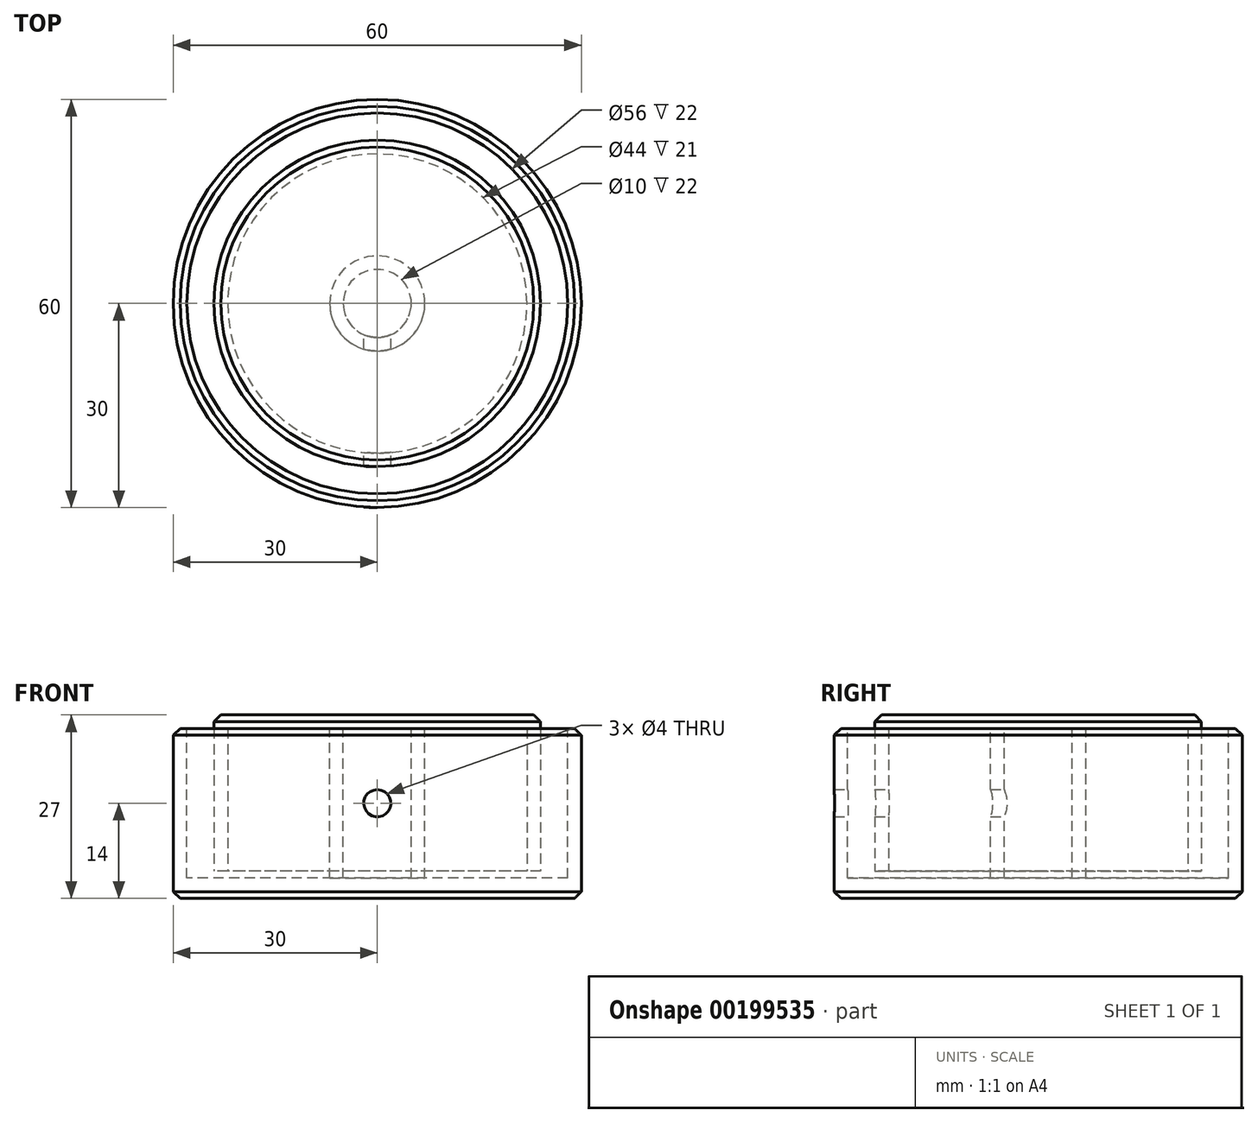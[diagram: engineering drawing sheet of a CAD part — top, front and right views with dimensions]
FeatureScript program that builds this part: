
annotation { "Feature Type Name" : "Feature", "Feature Type Description" : "" }
export const myFeature = defineFeature(function(context is Context, id is Id, definition is map)
    precondition{}
    {
        {
            var Q0;
            Q0=qCreatedBy(makeId("Top.planeOp"),FACE);
            var sketch = newSketch(context, id + "F0", { "sketchPlane" : qUnion([Q0])});
            skCircle(sketch, "E0", {"center": v(0, 0) * mm, "radius": 30 * mm});
            skSolve(sketch);
        }
        {
            var Q0;
            Q0 = qSketchRegion(id + "F0", true);
            extrude(context, id + "F1", {"entities" : qUnion([Q0]), "depth" : 25 * mm});
        }
        {
            var Q0;
            Q0=makeQuery(id+"F1.opExtrude","CAP_FACE",FACE,{"disambiguationData":[OSD([sQuery(id+"F0.wireOp",EDGE,"E0")])],"isStart":false});
            var sketch = newSketch(context, id + "F2", { "sketchPlane" : qUnion([Q0])});
            skCircle(sketch, "E1", {"center": v(0, 0) * mm, "radius": 28 * mm});
            skSolve(sketch);
        }
        {
            var Q0;
            Q0 = qSketchRegion(id + "F2", true);
            extrude(context, id + "F3", {"entities" : qUnion([Q0]), "operationType" : NewBodyOperationType.REMOVE, "oppositeDirection" : true, "depth" : 22 * mm});
        }
        {
            var Q0;
            Q0=makeQuery(id+"F3.boolean.opBoolean","COPY",FACE,{"derivedFrom":makeQuery(id+"F3.opExtrude","CAP_FACE",FACE,{"disambiguationData":[OSD([sQuery(id+"F2.wireOp",EDGE,"E1")])],"isStart":false})});
            cPlane(context, id + "F4", {"entities" : qUnion([Q0]), "cplaneType" : CPlaneType.OFFSET, "offset" : 1 * mm, "width" : 150 * mm, "height" : 150 * mm});
        }
        {
            var Q0;
            Q0=qCreatedBy(id+"F4.planeOp",FACE);
            var sketch = newSketch(context, id + "F5", { "sketchPlane" : qUnion([Q0])});
            skCircle(sketch, "E2", {"center": v(0, 0) * mm, "radius": 24 * mm});
            skCircle(sketch, "E3.0", {"center": v(0, 0) * mm, "radius": 22 * mm});
            skSolve(sketch);
        }
        {
            var Q0;
            Q0 = qSketchRegion(id + "F5", true);
            extrude(context, id + "F6", {"entities" : qUnion([Q0]), "depth" : 21 * mm});
        }
        {
            var Q0;
            Q0=makeQuery(id+"F6.opExtrude","CAP_FACE",FACE,{"disambiguationData":[OSD([sQuery(id+"F5.wireOp",EDGE,"E2"),sQuery(id+"F5.wireOp",EDGE,"E3.0")])],"isStart":false});
            var sketch = newSketch(context, id + "F7", { "sketchPlane" : qUnion([Q0])});
            skCircle(sketch, "E4", {"center": v(0, 0) * mm, "radius": 24 * mm});
            skSolve(sketch);
        }
        {
            var Q0;
            Q0 = qSketchRegion(id + "F7", true);
            extrude(context, id + "F8", {"entities" : qUnion([Q0]), "operationType" : NewBodyOperationType.ADD, "depth" : 2 * mm});
        }
        {
            var Q0;
            Q0=makeQuery(id+"F8.opExtrude","CAP_FACE",FACE,{"disambiguationData":[OSD([sQuery(id+"F7.wireOp",EDGE,"E4")])],"isStart":true});
            var sketch = newSketch(context, id + "F9", { "sketchPlane" : qUnion([Q0])});
            skCircle(sketch, "E5", {"center": v(0, 0) * mm, "radius": 5 * mm});
            skCircle(sketch, "E6.0", {"center": v(0, 0) * mm, "radius": 7 * mm});
            skSolve(sketch);
        }
        {
            var Q0;
            Q0 = qSketchRegion(id + "F9", true);
            extrude(context, id + "F10", {"entities" : qUnion([Q0]), "operationType" : NewBodyOperationType.ADD, "depth" : 22 * mm});
        }
        {
            var Q0;
            Q0=makeQuery(id+"F1.opExtrude","CAP_EDGE",EDGE,{"disambiguationData":[OSD([sQuery(id+"F0.wireOp",EDGE,"E0")])],"isStart":true});
            var Q1;
            Q1=makeQuery(id+"F8.opExtrude","CAP_EDGE",EDGE,{"disambiguationData":[OSD([sQuery(id+"F7.wireOp",EDGE,"E4")])],"isStart":false});
            var Q2;
            Q2=makeQuery(id+"F1.opExtrude","CAP_EDGE",EDGE,{"disambiguationData":[OSD([sQuery(id+"F0.wireOp",EDGE,"E0")])],"isStart":false});
            chamfer(context, id + "F11", {"entities" : qUnion([Q0, Q1, Q2]), "width" : 1 * mm, "tangentPropagation" : true});
        }
        {
            var Q0;
            Q0=qCreatedBy(makeId("Front.planeOp"),FACE);
            var sketch = newSketch(context, id + "F12", { "sketchPlane" : qUnion([Q0])});
            skCircle(sketch, "E7", {"center": v(0, 14) * mm, "radius": 1.38 * mm});
            skSolve(sketch);
        }
        {
            var Q0;
            Q0 = qSketchRegion(id + "F12", true);
            extrude(context, id + "F13", {"entities" : qUnion([Q0]), "operationType" : NewBodyOperationType.REMOVE, "endBound" : BoundingType.THROUGH_ALL, "depth" : 50 * mm});
        }
        {
            var Q0;
            Q0=qCreatedBy(makeId("Front.planeOp"),FACE);
            var sketch = newSketch(context, id + "F14", { "sketchPlane" : qUnion([Q0])});
            skCircle(sketch, "E8", {"center": v(0, 14) * mm, "radius": 2 * mm});
            skSolve(sketch);
        }
        {
            var Q0;
            Q0 = qSketchRegion(id + "F14", true);
            extrude(context, id + "F15", {"entities" : qUnion([Q0]), "operationType" : NewBodyOperationType.REMOVE, "endBound" : BoundingType.THROUGH_ALL, "depth" : 25 * mm});
        }
    });
